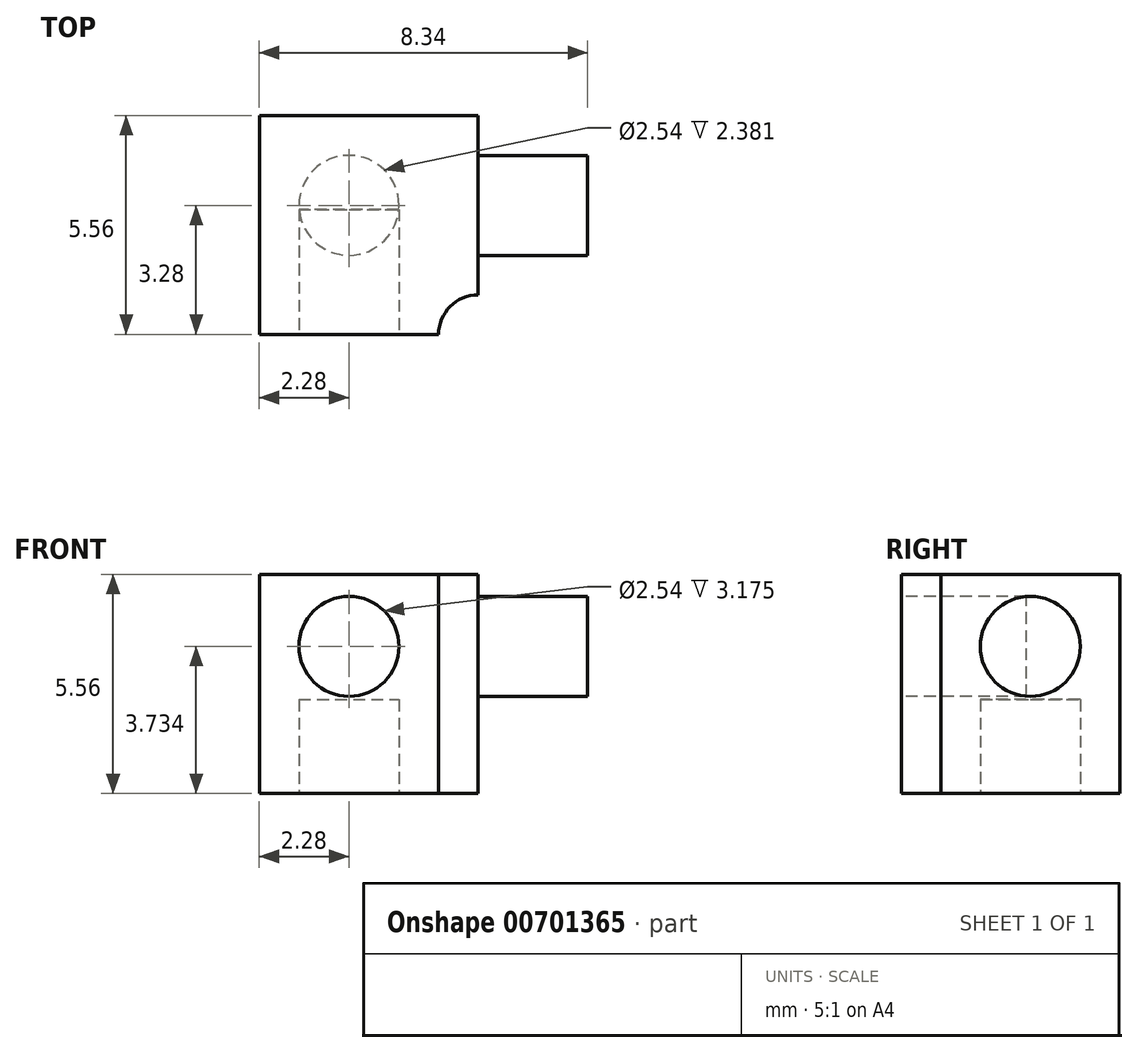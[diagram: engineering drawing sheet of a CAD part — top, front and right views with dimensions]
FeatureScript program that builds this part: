
annotation { "Feature Type Name" : "Feature", "Feature Type Description" : "" }
export const myFeature = defineFeature(function(context is Context, id is Id, definition is map)
    precondition{}
    {
        {
            var Q0;
            Q0=qCreatedBy(makeId("Top.planeOp"),FACE);
            var sketch = newSketch(context, id + "F0", { "sketchPlane" : qUnion([Q0])});
            skLineSegment(sketch, "E0.bottom", {"start": v(0, 0) * mm, "end": v(-5.56, 0) * mm});
            skLineSegment(sketch, "E0.top", {"start": v(0, 5.56) * mm, "end": v(-5.56, 5.56) * mm});
            skLineSegment(sketch, "E0.left", {"start": v(0, 0) * mm, "end": v(0, 5.56) * mm});
            skLineSegment(sketch, "E0.right", {"start": v(-5.56, 0) * mm, "end": v(-5.56, 5.56) * mm});
            skCircle(sketch, "E1", {"center": v(0, 0) * mm, "radius": 1 * mm});
            skSolve(sketch);
        }
        {
            var Q0;
            {var subQ2=sQuery(id+"F0.wireOp",EDGE,"E0.top");Q0=makeQuery(id+"F0.imprint","IMPRINT",FACE,{"disambiguationData":[TD([[makeQuery(id+"F0.imprint","IMPRINT",EDGE,{"derivedFrom":subQ2}),1.0]])]});}
            extrude(context, id + "F1", {"entities" : qUnion([Q0]), "depth" : 5.56 * mm, "offsetDistance" : 25.4 * mm});
        }
        {
            var Q0;
            Q0=makeQuery(id+"F1.opExtrude","SWEPT_FACE",FACE,{"disambiguationData":[OSD([sQuery(id+"F0.wireOp",EDGE,"E0.left")])]});
            var sketch = newSketch(context, id + "F2", { "sketchPlane" : qUnion([Q0])});
            skPoint(sketch, "E2.centerSnap0", {"position": v(3.28, 5.56) * mm});
            skPoint(sketch, "E2.centerSnap1", {"position": v(1, 2.78) * mm});
            skCircle(sketch, "E3", {"center": v(3.28, 3.73) * mm, "radius": 1.27 * mm});
            skSolve(sketch);
        }
        {
            var Q0;
            Q0=makeQuery(id+"F1.opExtrude","SWEPT_FACE",FACE,{"disambiguationData":[OSD([sQuery(id+"F0.wireOp",EDGE,"E0.bottom")])]});
            var sketch = newSketch(context, id + "F3", { "sketchPlane" : qUnion([Q0])});
            skPoint(sketch, "E4.centerSnap0", {"position": v(-1, 2.78) * mm});
            skPoint(sketch, "E4.centerSnap1", {"position": v(-3.28, 5.56) * mm});
            skCircle(sketch, "E5", {"center": v(-3.28, 3.73) * mm, "radius": 1.27 * mm});
            skSolve(sketch);
        }
        {
            var Q0;
            Q0=makeQuery(id+"F3.imprint","IMPRINT",FACE,{"disambiguationData":[TD([[makeQuery(id+"F3.imprint","IMPRINT",EDGE,{"derivedFrom":sQuery(id+"F3.wireOp",EDGE,"E5")}),1.0]])]});
            extrude(context, id + "F4", {"entities" : qUnion([Q0]), "operationType" : NewBodyOperationType.REMOVE, "oppositeDirection" : true, "depth" : 3.17 * mm, "offsetDistance" : 25.4 * mm});
        }
        {
            var Q0;
            Q0=makeQuery(id+"F1.opExtrude","CAP_FACE",FACE,{"disambiguationData":[OSD([sQuery(id+"F0.wireOp",EDGE,"E0.bottom"),sQuery(id+"F0.wireOp",EDGE,"E0.top"),sQuery(id+"F0.wireOp",EDGE,"E0.left"),sQuery(id+"F0.wireOp",EDGE,"E0.right"),sQuery(id+"F0.wireOp",EDGE,"E1")])],"isStart":true});
            var sketch = newSketch(context, id + "F5", { "sketchPlane" : qUnion([Q0])});
            skCircle(sketch, "E6", {"center": v(-3.28, -3.28) * mm, "radius": 1.27 * mm});
            skPoint(sketch, "E6.centerSnap0", {"position": v(0, -3.28) * mm});
            skPoint(sketch, "E6.centerSnap1", {"position": v(-3.28, 0) * mm});
            skSolve(sketch);
        }
        {
            var Q0;
            Q0=makeQuery(id+"F5.imprint","IMPRINT",FACE,{"disambiguationData":[TD([[makeQuery(id+"F5.imprint","IMPRINT",EDGE,{"derivedFrom":sQuery(id+"F5.wireOp",EDGE,"E6")}),1.0]])]});
            extrude(context, id + "F6", {"entities" : qUnion([Q0]), "operationType" : NewBodyOperationType.REMOVE, "oppositeDirection" : true, "depth" : 2.38 * mm, "offsetDistance" : 25.4 * mm});
        }
        {
            var Q0;
            Q0=makeQuery(id+"F2.imprint","IMPRINT",FACE,{"disambiguationData":[TD([[makeQuery(id+"F2.imprint","IMPRINT",EDGE,{"derivedFrom":sQuery(id+"F2.wireOp",EDGE,"E3")}),1.0]])]});
            extrude(context, id + "F7", {"entities" : qUnion([Q0]), "operationType" : NewBodyOperationType.ADD, "depth" : 2.78 * mm, "offsetDistance" : 25.4 * mm});
        }
        {
            var Q0;
            Q0=makeQuery(id+"F1.opExtrude","SWEPT_BODY",BODY,{"disambiguationData":[OSD([sQuery(id+"F0.wireOp",EDGE,"E0.bottom"),sQuery(id+"F0.wireOp",EDGE,"E0.top"),sQuery(id+"F0.wireOp",EDGE,"E0.left"),sQuery(id+"F0.wireOp",EDGE,"E0.right"),sQuery(id+"F0.wireOp",EDGE,"E1")])]});
            transform(context, id + "F8", {"entities" : qUnion([Q0]), "transformType" : TransformType.TRANSLATION_3D, "dx" : 25.4 * mm, "dy" : 0 * mm, "dz" : 0 * mm, "makeCopy" : true});
        }
        {
            var Q0;
            Q0=makeQuery(id+"F8.opPattern","COPY",BODY,{"derivedFrom":makeQuery(id+"F1.opExtrude","SWEPT_BODY",BODY,{"disambiguationData":[OSD([sQuery(id+"F0.wireOp",EDGE,"E0.bottom"),sQuery(id+"F0.wireOp",EDGE,"E0.top"),sQuery(id+"F0.wireOp",EDGE,"E0.left"),sQuery(id+"F0.wireOp",EDGE,"E0.right"),sQuery(id+"F0.wireOp",EDGE,"E1")])]}),"instanceName":"1"});
            deleteBodies(context, id + "F9", {"entities" : qUnion([Q0])});
        }
    });
